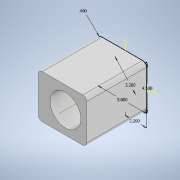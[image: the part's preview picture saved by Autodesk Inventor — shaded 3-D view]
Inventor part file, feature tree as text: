
AUTODESK INVENTOR PART (.ipt)
format: ipt  version: 2021.1 (Build 251245000, 245)  size: 118,784 bytes
history: native  units: in
note: dims shown in document units (in); Inventor stores cm internally (conversion verified against a paired STEP export)
features: extrude x2, sketch x1
ambient origin geometry x8: Origin, YZ Plane, XZ Plane, XY Plane, X Axis, Y Axis, Z Axis, Center Point
bodies: Solid1 (feature_tree)
feature tree (3):
  sketch  "Sketch1"  dims[d0=5.0in d1=4.5in d2=2.2in d3=0.4in d4=6.2in d5=0.0in d6=3.2in d7=6.2in d8=0.0in]
  extrude  "Extrusion1"  Depth=4.5in
  extrude  "Extrusion2"  Depth=6.2in
